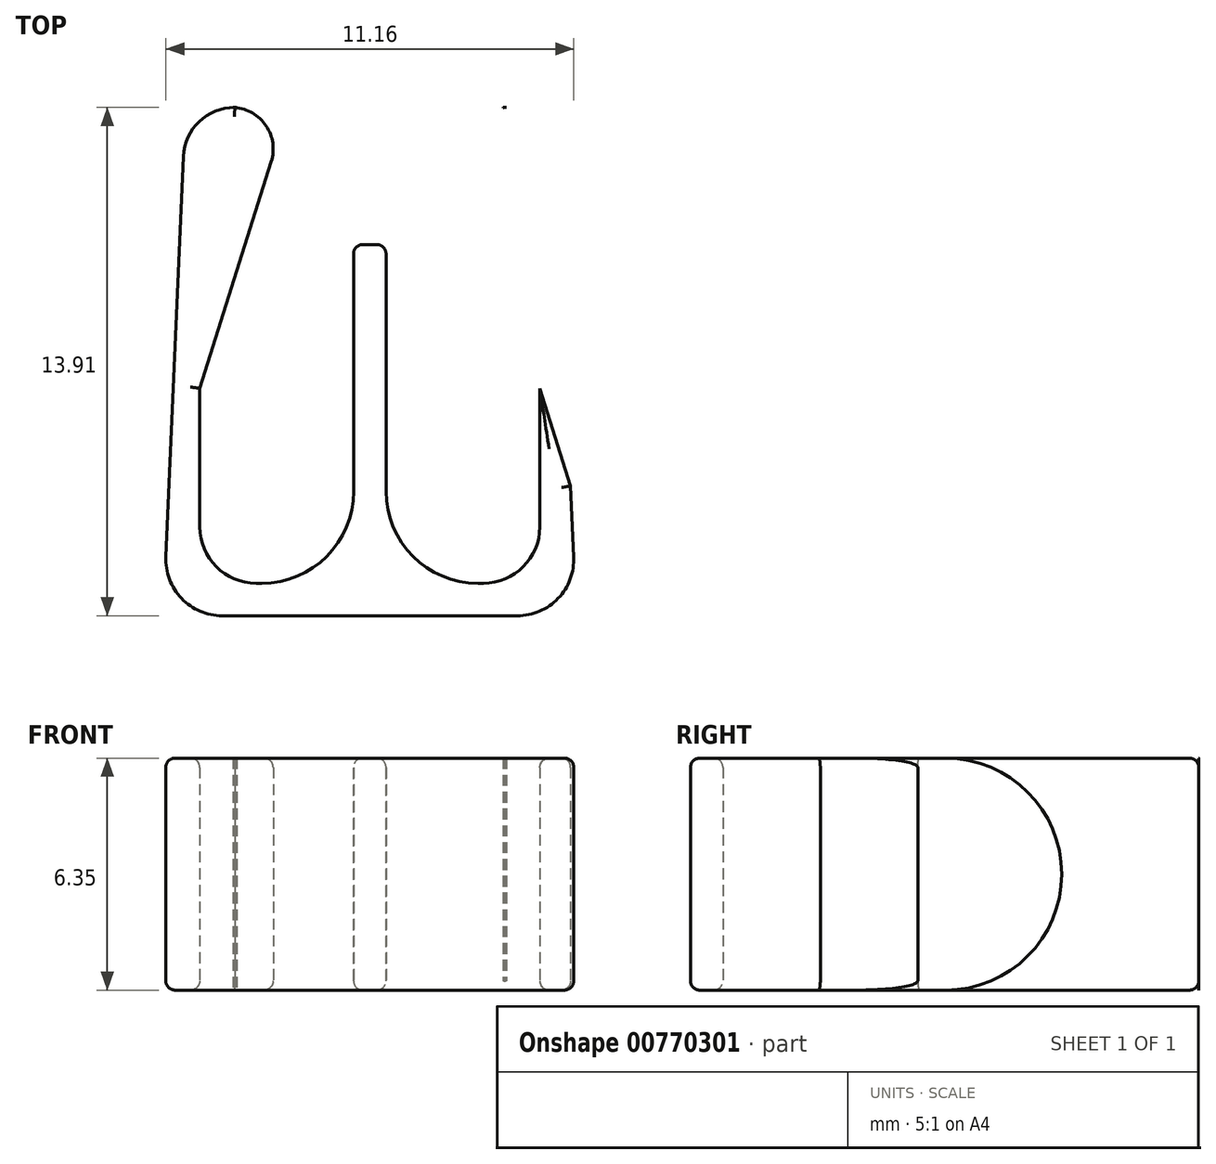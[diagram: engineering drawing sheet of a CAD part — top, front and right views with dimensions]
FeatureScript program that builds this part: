
annotation { "Feature Type Name" : "Feature", "Feature Type Description" : "" }
export const myFeature = defineFeature(function(context is Context, id is Id, definition is map)
    precondition{}
    {
        {
            var Q0;
            Q0=qCreatedBy(makeId("Top.planeOp"),FACE);
            var sketch = newSketch(context, id + "F0", { "sketchPlane" : qUnion([Q0])});
            skLineSegment(sketch, "E0", {"start": v(-5.1, 2.84) * mm, "end": v(-5.58, -8.12) * mm});
            skLineSegment(sketch, "E1", {"start": v(-4.04, -9.73) * mm, "end": v(0, -9.73) * mm});
            skLineSegment(sketch, "E2", {"start": v(0, -9.73) * mm, "end": v(0, 0.43) * mm});
            skLineSegment(sketch, "E3", {"start": v(-3.74, 4.18) * mm, "end": v(-3.65, 4.18) * mm});
            skLineSegment(sketch, "E4", {"start": v(-2.7, 2.7) * mm, "end": v(-5.5, -6.18) * mm});
            skPoint(sketch, "E5.visualSharp", {"position": v(-5.65, -9.73) * mm});
            skArc(sketch, "E5.filletArc", {"start": v(-5.58, -8.12) * mm, "mid": v(-5.15, -9.26) * mm, "end": v(-4.04, -9.73) * mm});
            skPoint(sketch, "E6.visualSharp", {"position": v(-5.04, 4.24) * mm});
            skArc(sketch, "E6.filletArc", {"start": v(-3.65, 4.18) * mm, "mid": v(-4.65, 3.81) * mm, "end": v(-5.1, 2.84) * mm});
            skPoint(sketch, "E7.visualSharp", {"position": v(-2.25, 4.12) * mm});
            skArc(sketch, "E7.filletArc", {"start": v(-2.7, 2.7) * mm, "mid": v(-2.85, 3.7) * mm, "end": v(-3.74, 4.18) * mm});
            skLineSegment(sketch, "E8", {"start": v(0, 0.43) * mm, "end": v(-0.44, 0.43) * mm});
            skLineSegment(sketch, "E9", {"start": v(-0.44, 0.43) * mm, "end": v(-0.44, -8.84) * mm});
            skLineSegment(sketch, "E10", {"start": v(-0.44, -8.84) * mm, "end": v(-3.1, -8.84) * mm});
            skLineSegment(sketch, "E11", {"start": v(-4.65, -7.3) * mm, "end": v(-4.65, -3.5) * mm});
            skPoint(sketch, "E12.visualSharp", {"position": v(-4.65, -8.84) * mm});
            skArc(sketch, "E12.filletArc", {"start": v(-4.65, -7.3) * mm, "mid": v(-4.2, -8.4) * mm, "end": v(-3.1, -8.84) * mm});
            skLineSegment(sketch, "E13", {"start": v(-5.65, -9.73) * mm, "end": v(-3.1, -7.3) * mm, "construction": true});
            skLineSegment(sketch, "E14.MirrorCS", {"start": v(3.74, 4.18) * mm, "end": v(3.65, 4.18) * mm});
            skArc(sketch, "E15.MirrorCS", {"start": v(3.65, 4.18) * mm, "mid": v(4.65, 3.81) * mm, "end": v(5.1, 2.84) * mm});
            skArc(sketch, "E16.MirrorCS", {"start": v(2.7, 2.7) * mm, "mid": v(2.85, 3.7) * mm, "end": v(3.74, 4.18) * mm});
            skLineSegment(sketch, "E17.MirrorCS", {"start": v(5.65, -9.73) * mm, "end": v(3.1, -7.3) * mm, "construction": true});
            skArc(sketch, "E18.MirrorCS", {"start": v(5.58, -8.12) * mm, "mid": v(5.15, -9.26) * mm, "end": v(4.04, -9.73) * mm});
            skLineSegment(sketch, "E19.MirrorCS", {"start": v(0, 0.43) * mm, "end": v(0.44, 0.43) * mm});
            skArc(sketch, "E20.MirrorCS", {"start": v(4.65, -7.3) * mm, "mid": v(4.2, -8.4) * mm, "end": v(3.1, -8.84) * mm});
            skLineSegment(sketch, "E21.MirrorCS", {"start": v(5.1, 2.84) * mm, "end": v(5.58, -8.12) * mm});
            skLineSegment(sketch, "E22.MirrorCS", {"start": v(4.04, -9.73) * mm, "end": v(0, -9.73) * mm});
            skLineSegment(sketch, "E23.MirrorCS", {"start": v(2.7, 2.7) * mm, "end": v(5.5, -6.18) * mm});
            skPoint(sketch, "E24.MirrorP", {"position": v(2.25, 4.12) * mm});
            skLineSegment(sketch, "E25.MirrorCS", {"start": v(0.44, 0.43) * mm, "end": v(0.44, -8.84) * mm});
            skLineSegment(sketch, "E26.MirrorCS", {"start": v(0.44, -8.84) * mm, "end": v(3.1, -8.84) * mm});
            skLineSegment(sketch, "E27.MirrorCS", {"start": v(4.65, -7.3) * mm, "end": v(4.65, -3.5) * mm});
            skPoint(sketch, "E28.MirrorP", {"position": v(5.65, -9.73) * mm});
            skPoint(sketch, "E29.MirrorP", {"position": v(5.04, 4.24) * mm});
            skPoint(sketch, "E30.MirrorP", {"position": v(4.65, -8.84) * mm});
            skSolve(sketch);
        }
        {
            var Q0;
            Q0=makeQuery(id+"F0.imprint","IMPRINT",FACE,{"disambiguationData":[TD([[makeQuery(id+"F0.imprint","IMPRINT",EDGE,{"derivedFrom":sQuery(id+"F0.wireOp",EDGE,"E2")}),-1.0]])]});
            var Q1;
            {var subQ4=sQuery(id+"F0.wireOp",EDGE,"E21.MirrorCS");var subQ5=sQuery(id+"F0.wireOp",EDGE,"E15.MirrorCS");var subQ6=makeQuery(id+"F0.imprint","INTERSECT",VERTEX,{"derivedFrom":[subQ5,subQ4]});Q1=makeQuery(id+"F0.imprint","IMPRINT",FACE,{"disambiguationData":[TD([[makeQuery(id+"F0.imprint","IMPRINT",EDGE,{"disambiguationData":[TD([[subQ6,1.0]])],"derivedFrom":subQ5}),-1.0]])]});}
            var Q2;
            {var subQ0=sQuery(id+"F0.wireOp",EDGE,"E6.filletArc");var subQ1=sQuery(id+"F0.wireOp",EDGE,"E0");var subQ2=makeQuery(id+"F0.imprint","INTERSECT",VERTEX,{"derivedFrom":[subQ1,subQ0]});Q2=makeQuery(id+"F0.imprint","IMPRINT",FACE,{"disambiguationData":[TD([[makeQuery(id+"F0.imprint","IMPRINT",EDGE,{"disambiguationData":[TD([[subQ2,-1.0]])],"derivedFrom":subQ1}),1.0]])]});}
            var Q3;
            {var subQ0=sQuery(id+"F0.wireOp",EDGE,"E3");Q3=makeQuery(id+"F0.imprint","IMPRINT",FACE,{"disambiguationData":[TD([[makeQuery(id+"F0.imprint","IMPRINT",EDGE,{"derivedFrom":subQ0}),-1.0]])]});}
            var Q4;
            {var subQ0=sQuery(id+"F0.wireOp",EDGE,"E14.MirrorCS");Q4=makeQuery(id+"F0.imprint","IMPRINT",FACE,{"disambiguationData":[TD([[makeQuery(id+"F0.imprint","IMPRINT",EDGE,{"derivedFrom":subQ0}),1.0]])]});}
            var Q5;
            Q5=makeQuery(id+"F0.imprint","IMPRINT",FACE,{"disambiguationData":[TD([[makeQuery(id+"F0.imprint","IMPRINT",EDGE,{"derivedFrom":sQuery(id+"F0.wireOp",EDGE,"E1")}),1.0]])]});
            extrude(context, id + "F1", {"entities" : qUnion([Q0, Q1, Q2, Q3, Q4, Q5]), "depth" : 6.35 * mm, "offsetDistance" : 25.4 * mm});
        }
        {
            var Q0;
            Q0=makeQuery(id+"F1.opExtrude","CAP_EDGE",EDGE,{"disambiguationData":[OSD([sQuery(id+"F0.wireOp",EDGE,"E8"),sQuery(id+"F0.wireOp",EDGE,"E19.MirrorCS")])],"isStart":false});
            var Q1;
            Q1=makeQuery(id+"F1.opExtrude","CAP_EDGE",EDGE,{"disambiguationData":[OSD([sQuery(id+"F0.wireOp",EDGE,"E8"),sQuery(id+"F0.wireOp",EDGE,"E19.MirrorCS")])],"isStart":true});
            fillet(context, id + "F2", {"entities" : qUnion([Q0, Q1]), "radius" : 3.17 * mm, "tangentPropagation" : true, "allowEdgeOverflow" : false});
        }
        {
            var Q0;
            Q0=makeQuery(id+"F1.opExtrude","SWEPT_EDGE",EDGE,{"disambiguationData":[OSD([sQuery(id+"F0.wireOp",EDGE,"E9"),sQuery(id+"F0.wireOp",EDGE,"E10")])]});
            var Q1;
            Q1=makeQuery(id+"F1.opExtrude","SWEPT_EDGE",EDGE,{"disambiguationData":[OSD([sQuery(id+"F0.wireOp",EDGE,"E25.MirrorCS"),sQuery(id+"F0.wireOp",EDGE,"E26.MirrorCS")])]});
            fillet(context, id + "F3", {"entities" : qUnion([Q0, Q1]), "radius" : 2.5 * mm, "tangentPropagation" : true, "allowEdgeOverflow" : false});
        }
        {
            var Q0;
            Q0=makeQuery(id+"F1.opExtrude","CAP_EDGE",EDGE,{"disambiguationData":[OSD([sQuery(id+"F0.wireOp",EDGE,"E23.MirrorCS")])],"isStart":true});
            var Q1;
            Q1=makeQuery(id+"F1.opExtrude","CAP_EDGE",EDGE,{"disambiguationData":[OSD([sQuery(id+"F0.wireOp",EDGE,"E21.MirrorCS")])],"isStart":true});
            var Q2;
            {var subQ0=sQuery(id+"F0.wireOp",EDGE,"E15.MirrorCS");Q2=makeQuery(id+"F1.opExtrude","CAP_EDGE",EDGE,{"disambiguationData":[OSD([subQ0]),TDD([makeQuery(id+"F0.imprint","IMPRINT",EDGE,{"disambiguationData":[TD([[makeQuery(id+"F0.imprint","INTERSECT",VERTEX,{"derivedFrom":[subQ0,sQuery(id+"F0.wireOp",EDGE,"E21.MirrorCS")]}),1.0]])],"derivedFrom":subQ0})])],"isStart":true});}
            var Q3;
            {var subQ0=sQuery(id+"F0.wireOp",EDGE,"E16.MirrorCS");Q3=makeQuery(id+"F1.opExtrude","CAP_EDGE",EDGE,{"disambiguationData":[OSD([subQ0]),TDD([makeQuery(id+"F0.imprint","IMPRINT",EDGE,{"disambiguationData":[TD([[makeQuery(id+"F0.imprint","INTERSECT",VERTEX,{"derivedFrom":[subQ0,sQuery(id+"F0.wireOp",EDGE,"E23.MirrorCS")]}),-1.0]])],"derivedFrom":subQ0})])],"isStart":true});}
            var Q4;
            Q4=makeQuery(id+"F1.opExtrude","CAP_EDGE",EDGE,{"disambiguationData":[OSD([sQuery(id+"F0.wireOp",EDGE,"E27.MirrorCS")])],"isStart":true});
            var Q5;
            Q5=makeQuery(id+"F1.opExtrude","CAP_EDGE",EDGE,{"disambiguationData":[OSD([sQuery(id+"F0.wireOp",EDGE,"E20.MirrorCS")])],"isStart":true});
            var Q6;
            Q6=makeQuery(id+"F1.opExtrude","CAP_FACE",FACE,{"disambiguationData":[OSD([sQuery(id+"F0.wireOp",EDGE,"E0"),sQuery(id+"F0.wireOp",EDGE,"E1"),sQuery(id+"F0.wireOp",EDGE,"E4"),sQuery(id+"F0.wireOp",EDGE,"E5.filletArc"),sQuery(id+"F0.wireOp",EDGE,"E6.filletArc"),sQuery(id+"F0.wireOp",EDGE,"E7.filletArc"),sQuery(id+"F0.wireOp",EDGE,"E8"),sQuery(id+"F0.wireOp",EDGE,"E9"),sQuery(id+"F0.wireOp",EDGE,"E10"),sQuery(id+"F0.wireOp",EDGE,"E11"),sQuery(id+"F0.wireOp",EDGE,"E12.filletArc"),sQuery(id+"F0.wireOp",EDGE,"E15.MirrorCS"),sQuery(id+"F0.wireOp",EDGE,"E16.MirrorCS"),sQuery(id+"F0.wireOp",EDGE,"E18.MirrorCS"),sQuery(id+"F0.wireOp",EDGE,"E19.MirrorCS"),sQuery(id+"F0.wireOp",EDGE,"E20.MirrorCS"),sQuery(id+"F0.wireOp",EDGE,"E21.MirrorCS"),sQuery(id+"F0.wireOp",EDGE,"E22.MirrorCS"),sQuery(id+"F0.wireOp",EDGE,"E23.MirrorCS"),sQuery(id+"F0.wireOp",EDGE,"E25.MirrorCS"),sQuery(id+"F0.wireOp",EDGE,"E26.MirrorCS"),sQuery(id+"F0.wireOp",EDGE,"E27.MirrorCS")])],"isStart":true});
            var Q7;
            Q7=makeQuery(id+"F1.opExtrude","CAP_FACE",FACE,{"disambiguationData":[OSD([sQuery(id+"F0.wireOp",EDGE,"E0"),sQuery(id+"F0.wireOp",EDGE,"E1"),sQuery(id+"F0.wireOp",EDGE,"E4"),sQuery(id+"F0.wireOp",EDGE,"E5.filletArc"),sQuery(id+"F0.wireOp",EDGE,"E6.filletArc"),sQuery(id+"F0.wireOp",EDGE,"E7.filletArc"),sQuery(id+"F0.wireOp",EDGE,"E8"),sQuery(id+"F0.wireOp",EDGE,"E9"),sQuery(id+"F0.wireOp",EDGE,"E10"),sQuery(id+"F0.wireOp",EDGE,"E11"),sQuery(id+"F0.wireOp",EDGE,"E12.filletArc"),sQuery(id+"F0.wireOp",EDGE,"E15.MirrorCS"),sQuery(id+"F0.wireOp",EDGE,"E16.MirrorCS"),sQuery(id+"F0.wireOp",EDGE,"E18.MirrorCS"),sQuery(id+"F0.wireOp",EDGE,"E19.MirrorCS"),sQuery(id+"F0.wireOp",EDGE,"E20.MirrorCS"),sQuery(id+"F0.wireOp",EDGE,"E21.MirrorCS"),sQuery(id+"F0.wireOp",EDGE,"E22.MirrorCS"),sQuery(id+"F0.wireOp",EDGE,"E23.MirrorCS"),sQuery(id+"F0.wireOp",EDGE,"E25.MirrorCS"),sQuery(id+"F0.wireOp",EDGE,"E26.MirrorCS"),sQuery(id+"F0.wireOp",EDGE,"E27.MirrorCS")])],"isStart":false});
            fillet(context, id + "F4", {"entities" : qUnion([Q0, Q1, Q2, Q3, Q4, Q5, Q6, Q7]), "radius" : 0.25 * mm, "tangentPropagation" : true, "allowEdgeOverflow" : false});
        }
    });
